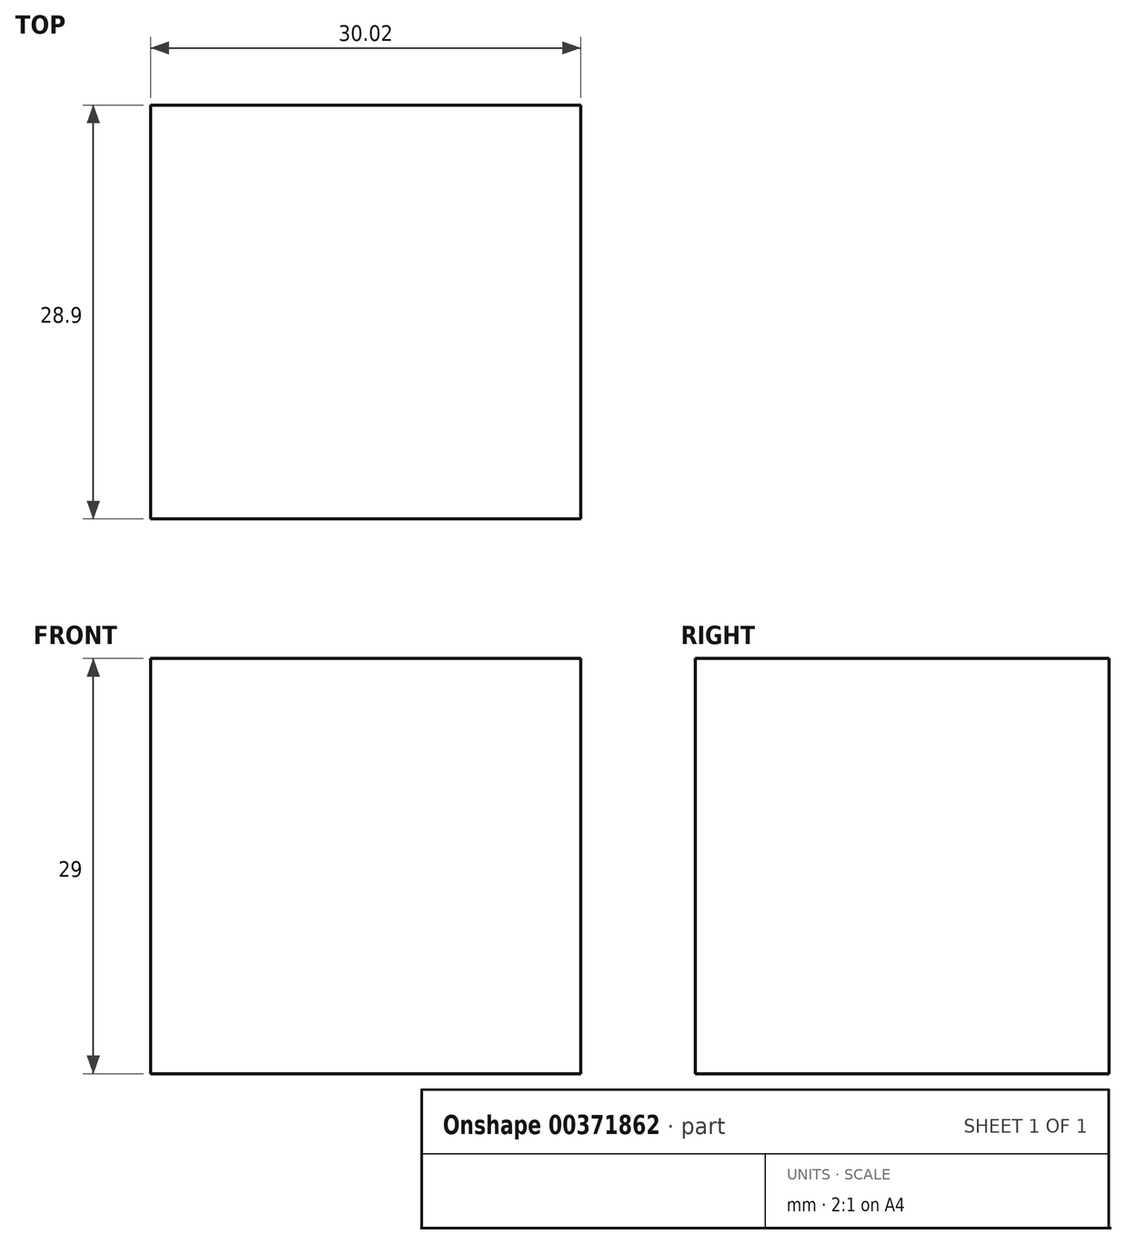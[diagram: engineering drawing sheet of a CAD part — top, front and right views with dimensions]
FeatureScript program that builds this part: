
annotation { "Feature Type Name" : "Feature", "Feature Type Description" : "" }
export const myFeature = defineFeature(function(context is Context, id is Id, definition is map)
    precondition{}
    {
        {
            var Q0;
            Q0=qCreatedBy(makeId("Top.planeOp"),FACE);
            var sketch = newSketch(context, id + "F0", { "sketchPlane" : qUnion([Q0])});
            skLineSegment(sketch, "E0.bottom", {"start": v(-23.8, 41.36) * mm, "end": v(6.23, 41.36) * mm});
            skLineSegment(sketch, "E0.top", {"start": v(-23.8, 12.46) * mm, "end": v(6.23, 12.46) * mm});
            skLineSegment(sketch, "E0.left", {"start": v(-23.8, 41.36) * mm, "end": v(-23.8, 12.46) * mm});
            skLineSegment(sketch, "E0.right", {"start": v(6.23, 41.36) * mm, "end": v(6.23, 12.46) * mm});
            skLineSegment(sketch, "E1.bottom", {"start": v(-23.8, 12.46) * mm, "end": v(-23.8, 12.46) * mm});
            skSolve(sketch);
        }
        {
            var Q0;
            Q0 = qSketchRegion(id + "F0", true);
            extrude(context, id + "F1", {"entities" : qUnion([Q0]), "depth" : 29 * mm});
        }
    });
